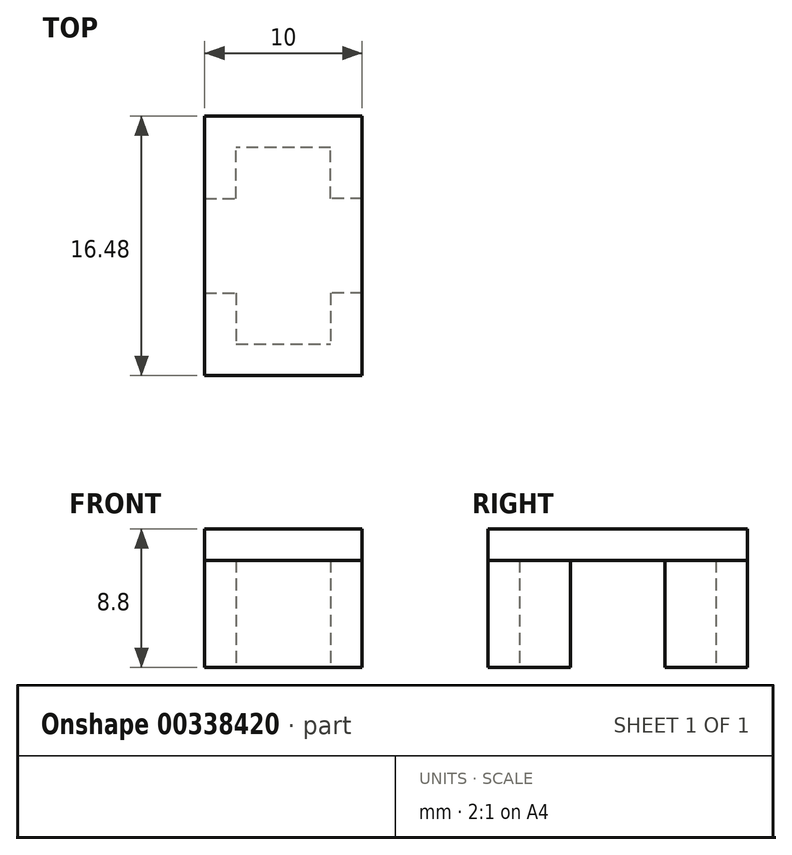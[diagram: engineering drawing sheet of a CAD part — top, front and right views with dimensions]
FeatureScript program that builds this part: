
annotation { "Feature Type Name" : "Feature", "Feature Type Description" : "" }
export const myFeature = defineFeature(function(context is Context, id is Id, definition is map)
    precondition{}
    {
        {
            var Q0;
            Q0=qCreatedBy(makeId("Top.planeOp"),FACE);
            var sketch = newSketch(context, id + "F0", { "sketchPlane" : qUnion([Q0])});
            skLineSegment(sketch, "E0.bottom", {"start": v(-5, 0) * mm, "end": v(-3, 0) * mm});
            skLineSegment(sketch, "E0.top", {"start": v(-5, 5.24) * mm, "end": v(0, 5.24) * mm});
            skLineSegment(sketch, "E0.left", {"start": v(-5, 0) * mm, "end": v(-5, 5.24) * mm});
            skLineSegment(sketch, "E1.top", {"start": v(0, 3.24) * mm, "end": v(-3, 3.24) * mm});
            skLineSegment(sketch, "E1.right", {"start": v(-3, 0) * mm, "end": v(-3, 3.24) * mm});
            skLineSegment(sketch, "E2.MirrorCS", {"start": v(5, 0) * mm, "end": v(5, 5.24) * mm});
            skLineSegment(sketch, "E3.MirrorCS", {"start": v(5, 5.24) * mm, "end": v(0, 5.24) * mm});
            skLineSegment(sketch, "E4.MirrorCS", {"start": v(0, 3.24) * mm, "end": v(3, 3.24) * mm});
            skLineSegment(sketch, "E5.MirrorCS", {"start": v(3, 0) * mm, "end": v(3, 3.24) * mm});
            skLineSegment(sketch, "E6.MirrorCS", {"start": v(5, 0) * mm, "end": v(3, 0) * mm});
            skLineSegment(sketch, "E7", {"start": v(-14.2, -3) * mm, "end": v(13.93, -3) * mm, "construction": true});
            skLineSegment(sketch, "E8.MirrorCS", {"start": v(-5, -6) * mm, "end": v(-3, -6) * mm});
            skLineSegment(sketch, "E9.MirrorCS", {"start": v(-5, -6) * mm, "end": v(-5, -11.24) * mm});
            skLineSegment(sketch, "E10.MirrorCS", {"start": v(-5, -11.24) * mm, "end": v(0, -11.24) * mm});
            skLineSegment(sketch, "E11.MirrorCS", {"start": v(5, -11.24) * mm, "end": v(0, -11.24) * mm});
            skLineSegment(sketch, "E12.MirrorCS", {"start": v(5, -6) * mm, "end": v(5, -11.24) * mm});
            skLineSegment(sketch, "E13.MirrorCS", {"start": v(5, -6) * mm, "end": v(3, -6) * mm});
            skLineSegment(sketch, "E14.MirrorCS", {"start": v(3, -6) * mm, "end": v(3, -9.24) * mm});
            skLineSegment(sketch, "E15.MirrorCS", {"start": v(0, -9.24) * mm, "end": v(3, -9.24) * mm});
            skLineSegment(sketch, "E16.MirrorCS", {"start": v(0, -9.24) * mm, "end": v(-3, -9.24) * mm});
            skLineSegment(sketch, "E17.MirrorCS", {"start": v(-3, -6) * mm, "end": v(-3, -9.24) * mm});
            skSolve(sketch);
        }
        {
            var Q0;
            Q0=qSketchRegion(id+"F0",true);
            extrude(context, id + "F1", {"entities" : qUnion([Q0]), "depth" : 6.8 * mm});
        }
        {
            var Q0;
            Q0=makeQuery(id+"F1.opExtrude","CAP_FACE",FACE,{"disambiguationData":[OSD([sQuery(id+"F0.wireOp",EDGE,"E0.bottom"),sQuery(id+"F0.wireOp",EDGE,"E0.top"),sQuery(id+"F0.wireOp",EDGE,"E0.left"),sQuery(id+"F0.wireOp",EDGE,"E1.top"),sQuery(id+"F0.wireOp",EDGE,"E1.right"),sQuery(id+"F0.wireOp",EDGE,"E2.MirrorCS"),sQuery(id+"F0.wireOp",EDGE,"E3.MirrorCS"),sQuery(id+"F0.wireOp",EDGE,"E4.MirrorCS"),sQuery(id+"F0.wireOp",EDGE,"E5.MirrorCS"),sQuery(id+"F0.wireOp",EDGE,"E6.MirrorCS")])],"isStart":false});
            var sketch = newSketch(context, id + "F2", { "sketchPlane" : qUnion([Q0])});
            skLineSegment(sketch, "E18.bottom", {"start": v(-5, 5.24) * mm, "end": v(5, 5.24) * mm});
            skLineSegment(sketch, "E18.top", {"start": v(-5, -11.24) * mm, "end": v(5, -11.24) * mm});
            skLineSegment(sketch, "E18.left", {"start": v(-5, 5.24) * mm, "end": v(-5, -11.24) * mm});
            skLineSegment(sketch, "E18.right", {"start": v(5, 5.24) * mm, "end": v(5, -11.24) * mm});
            skSolve(sketch);
        }
        {
            var Q0;
            {var subQ2=sQuery(id+"F2.wireOp",EDGE,"E18.top");Q0=makeQuery(id+"F2.imprint","IMPRINT",FACE,{"disambiguationData":[TD([[makeQuery(id+"F2.imprint","IMPRINT",EDGE,{"derivedFrom":subQ2}),1.0]])]});}
            var Q1;
            {var subQ3=sQuery(id+"F2.wireOp",EDGE,"E18.bottom");Q1=makeQuery(id+"F2.imprint","IMPRINT",FACE,{"disambiguationData":[TD([[makeQuery(id+"F2.imprint","IMPRINT",EDGE,{"derivedFrom":subQ3}),1.0]])]});}
            extrude(context, id + "F3", {"entities" : qUnion([Q0, Q1]), "depth" : 2 * mm});
        }
    });
